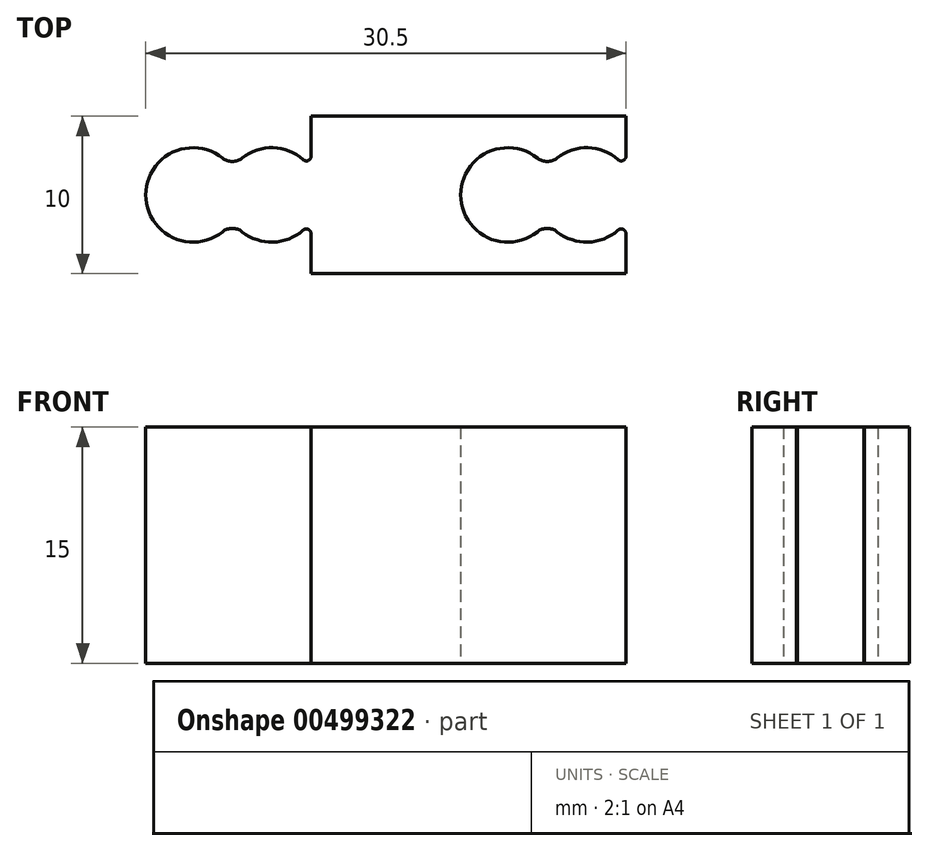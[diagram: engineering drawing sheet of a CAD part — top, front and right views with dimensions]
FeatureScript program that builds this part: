
annotation { "Feature Type Name" : "Feature", "Feature Type Description" : "" }
export const myFeature = defineFeature(function(context is Context, id is Id, definition is map)
    precondition{}
    {
        {
            var Q0;
            Q0=qCreatedBy(makeId("Top.planeOp"),FACE);
            var sketch = newSketch(context, id + "F0", { "sketchPlane" : qUnion([Q0])});
            skLineSegment(sketch, "E0", {"start": v(-28.89, 0) * mm, "end": v(20.55, 0) * mm, "construction": true});
            skLineSegment(sketch, "E1", {"start": v(0, 15.76) * mm, "end": v(0, -17.69) * mm, "construction": true});
            skLineSegment(sketch, "E2.bottom", {"start": v(10, -5) * mm, "end": v(-10, -5) * mm});
            skLineSegment(sketch, "E2.top", {"start": v(10, 5) * mm, "end": v(-10, 5) * mm});
            skLineSegment(sketch, "E2.left", {"start": v(10, -5) * mm, "end": v(10, -2.46) * mm});
            skLineSegment(sketch, "E2.right", {"start": v(-10, -5) * mm, "end": v(-10, -2.46) * mm});
            skPoint(sketch, "E2.middle", {"position": v(0, 0) * mm});
            skArc(sketch, "E3", {"start": v(5.62, -2.34) * mm, "mid": v(7.58, -3) * mm, "end": v(9.5, -2.24) * mm});
            skArc(sketch, "E4", {"start": v(4.37, 2.34) * mm, "mid": v(-0.5, 0) * mm, "end": v(4.37, -2.34) * mm});
            skArc(sketch, "E5.trimOffspring", {"start": v(9.5, 2.24) * mm, "mid": v(7.58, 3) * mm, "end": v(5.62, 2.34) * mm});
            skLineSegment(sketch, "E6.trimOffspring", {"start": v(10, 2.46) * mm, "end": v(10, 5) * mm});
            skPoint(sketch, "E7.visualSharp", {"position": v(5, 1.66) * mm});
            skArc(sketch, "E7.filletArc", {"start": v(4.37, 2.34) * mm, "mid": v(5, 2.12) * mm, "end": v(5.62, 2.34) * mm});
            skPoint(sketch, "E8.visualSharp", {"position": v(5, -1.66) * mm});
            skArc(sketch, "E8.filletArc", {"start": v(5.62, -2.34) * mm, "mid": v(5, -2.12) * mm, "end": v(4.37, -2.34) * mm});
            skPoint(sketch, "E9.visualSharp", {"position": v(10, 1.66) * mm});
            skArc(sketch, "E9.filletArc", {"start": v(9.5, 2.24) * mm, "mid": v(9.82, 2.19) * mm, "end": v(10, 2.46) * mm});
            skPoint(sketch, "E10.visualSharp", {"position": v(10, -1.66) * mm});
            skArc(sketch, "E10.filletArc", {"start": v(10, -2.46) * mm, "mid": v(9.82, -2.19) * mm, "end": v(9.5, -2.24) * mm});
            skArc(sketch, "E11.1.0.0", {"start": v(-14.38, -2.34) * mm, "mid": v(-12.42, -3) * mm, "end": v(-10.5, -2.24) * mm});
            skPoint(sketch, "E11.1.0.1", {"position": v(-15, 1.66) * mm});
            skPoint(sketch, "E11.1.0.2", {"position": v(-15, -1.66) * mm});
            skArc(sketch, "E11.1.0.3", {"start": v(-15.63, 2.34) * mm, "mid": v(-20.5, 0) * mm, "end": v(-15.63, -2.34) * mm});
            skArc(sketch, "E11.1.0.4", {"start": v(-10.5, 2.24) * mm, "mid": v(-12.42, 3) * mm, "end": v(-14.38, 2.34) * mm});
            skPoint(sketch, "E11.1.0.5", {"position": v(-10, 1.66) * mm});
            skPoint(sketch, "E11.1.0.7", {"position": v(-10, -1.66) * mm});
            skArc(sketch, "E11.1.0.8", {"start": v(-15.62, 2.34) * mm, "mid": v(-15, 2.12) * mm, "end": v(-14.38, 2.34) * mm});
            skArc(sketch, "E11.1.0.9", {"start": v(-14.38, -2.34) * mm, "mid": v(-15, -2.12) * mm, "end": v(-15.62, -2.34) * mm});
            skArc(sketch, "E11.1.0.10", {"start": v(-10.5, 2.24) * mm, "mid": v(-10.18, 2.19) * mm, "end": v(-10, 2.46) * mm});
            skArc(sketch, "E11.1.0.11", {"start": v(-10, -2.46) * mm, "mid": v(-10.18, -2.19) * mm, "end": v(-10.5, -2.24) * mm});
            skLineSegment(sketch, "E12.trimOffspring", {"start": v(-10, 2.46) * mm, "end": v(-10, 5) * mm});
            skLineSegment(sketch, "E13.direction1", {"start": v(-28.89, 0) * mm, "end": v(11.11, 0) * mm, "construction": true});
            skSolve(sketch);
        }
        {
            var Q0;
            Q0=makeQuery(id+"F0.imprint","IMPRINT",FACE,{"disambiguationData":[TD([[makeQuery(id+"F0.imprint","IMPRINT",EDGE,{"derivedFrom":sQuery(id+"F0.wireOp",EDGE,"E2.bottom")}),-1.0]])]});
            extrude(context, id + "F1", {"entities" : qUnion([Q0]), "depth" : 15 * mm});
        }
    });
